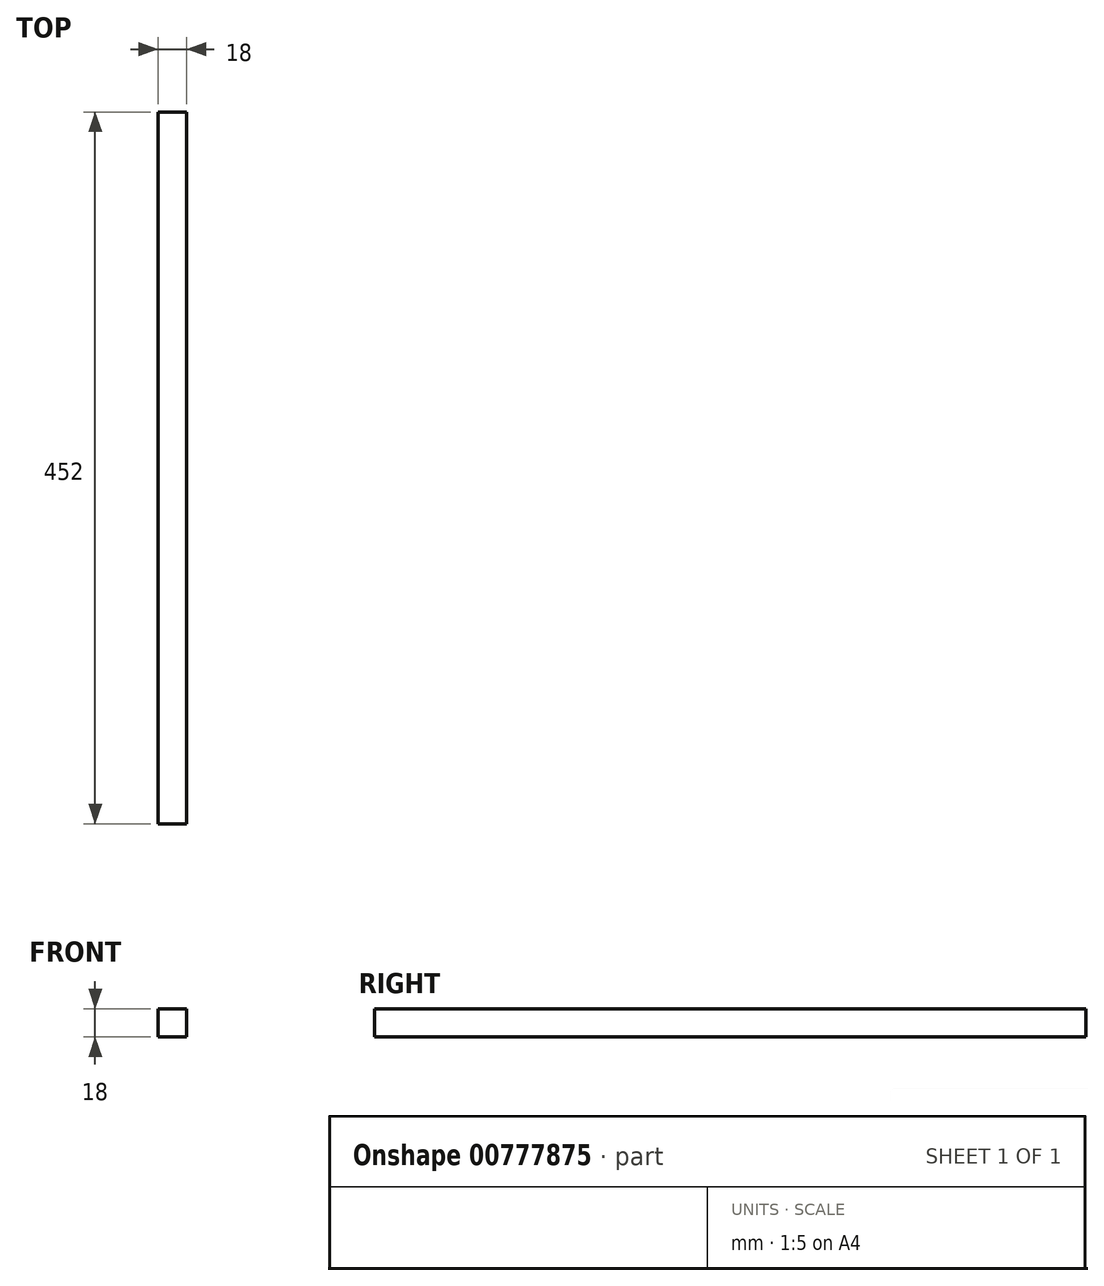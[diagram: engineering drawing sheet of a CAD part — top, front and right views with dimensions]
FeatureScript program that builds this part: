
annotation { "Feature Type Name" : "Feature", "Feature Type Description" : "" }
export const myFeature = defineFeature(function(context is Context, id is Id, definition is map)
    precondition{}
    {
        {
            var Q0;
            Q0=qCreatedBy(makeId("Top.planeOp"),FACE);
            var sketch = newSketch(context, id + "F0", { "sketchPlane" : qUnion([Q0])});
            skLineSegment(sketch, "E0.bottom", {"start": v(-9, 226) * mm, "end": v(9, 226) * mm});
            skLineSegment(sketch, "E0.top", {"start": v(-9, -226) * mm, "end": v(9, -226) * mm});
            skLineSegment(sketch, "E0.left", {"start": v(-9, 226) * mm, "end": v(-9, -226) * mm});
            skLineSegment(sketch, "E0.right", {"start": v(9, 226) * mm, "end": v(9, -226) * mm});
            skSolve(sketch);
        }
        {
            var Q0;
            Q0 = qSketchRegion(id + "F0", true);
            extrude(context, id + "F1", {"entities" : qUnion([Q0]), "endBound" : BoundingType.SYMMETRIC, "depth" : 18 * mm, "offsetDistance" : 25 * mm});
        }
    });
